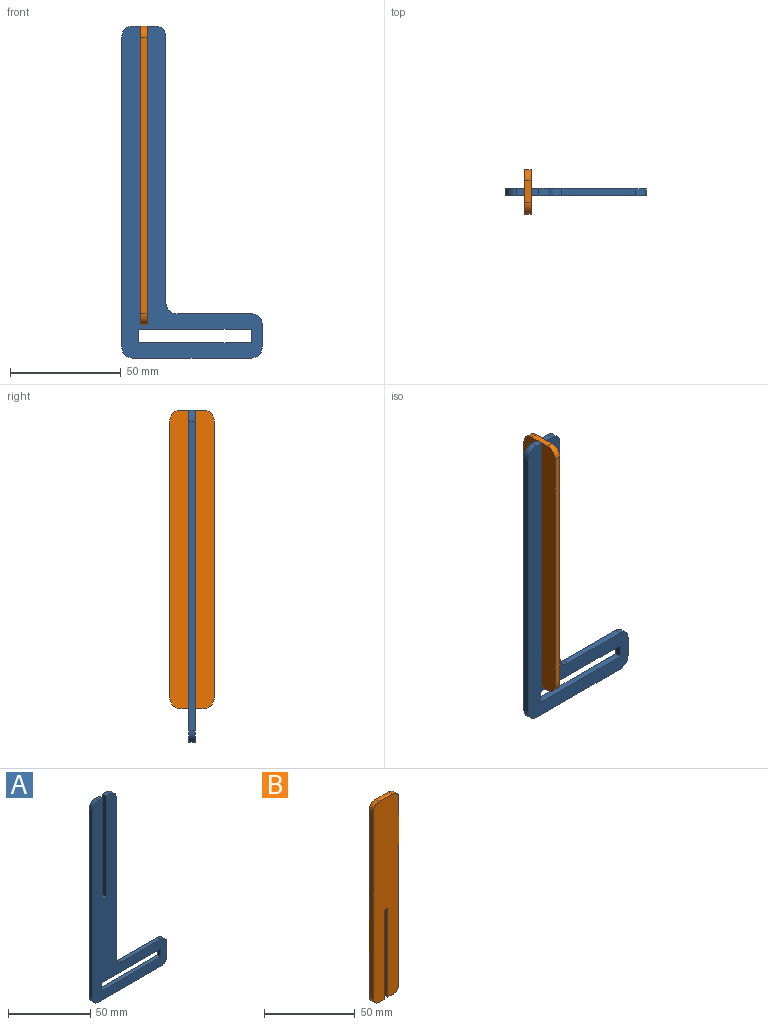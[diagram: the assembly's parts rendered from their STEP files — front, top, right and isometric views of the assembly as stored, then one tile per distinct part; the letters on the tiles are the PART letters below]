
ASSEMBLY  parts=2 mates=1
PART A: 22 faces, bbox 63.5x3x150 mm
  f0: plane 53.5x3mm, normal (0,0,-1), area 160.5mm2, adj f14,f15,f16,f21
  f1: plane 10x3mm, normal (1,0,0), area 30mm2, adj f14,f15,f16,f17
  f2: plane 33.5x3mm, normal (0,0,1), area 100.5mm2, adj f14,f15,f17,f18
  f3: plane 120x3mm, normal (1,0,0), area 360mm2, adj f14,f15,f18,f19
  f4: plane 3.5x3mm, normal (0,0,1), area 10.5mm2, adj f5,f14,f15,f19
  f5: plane 75x3mm, normal (-1,0,0), area 225mm2, adj f4,f6,f14,f15
  f6: plane 3x3mm, normal (0,0,1), area 9mm2, adj f5,f7,f14,f15
  f7: plane 75x3mm, normal (1,0,0), area 225mm2, adj f6,f8,f14,f15
  f8: plane 3.5x3mm, normal (0,0,1), area 10.5mm2, adj f7,f14,f15,f20
  f9: plane 6x3mm, normal (-1,0,0), area 18mm2, adj f10,f12,f14,f15
  f10: plane 51x3mm, normal (0,0,1), area 153mm2, adj f9,f11,f14,f15
  f11: plane 6x3mm, normal (1,0,0), area 18mm2, adj f10,f12,f14,f15
  f12: plane 51x3mm, normal (0,0,-1), area 153mm2, adj f9,f11,f14,f15
  f13: plane 140x3mm, normal (-1,0,0), area 420mm2, adj f14,f15,f20,f21
  f14: plane 150x63.5mm, normal (0,-1,0), area 3317.5mm2, adj f0,f1,f2,f3,f4,f5,f6,f7
  f15: plane 150x63.5mm, normal (0,1,0), area 3317.5mm2, adj f0,f1,f2,f3,f4,f5,f6,f7
  f16: cylinder r=5mm len=5mm, axis (0,1,0), area 23.6mm2, adj f0,f1,f14,f15
  f17: cylinder r=5mm len=5mm, axis (0,1,0), area 23.6mm2, adj f1,f2,f14,f15
  f18: cylinder r=5mm len=5mm, axis (0,-1,0), area 23.6mm2, adj f2,f3,f14,f15
  f19: cylinder r=5mm len=5mm, axis (0,-1,0), area 23.6mm2, adj f3,f4,f14,f15
  f20: cylinder r=5mm len=5mm, axis (0,-1,0), area 23.6mm2, adj f8,f13,f14,f15
  f21: cylinder r=5mm len=5mm, axis (0,1,0), area 23.6mm2, adj f0,f13,f14,f15
PART B: 14 faces, bbox 20x3x135 mm
  f0: plane 10x3mm, normal (0,0,1), area 30mm2, adj f8,f9,f10,f13
  f1: plane 125x3mm, normal (-1,0,0), area 375mm2, adj f8,f9,f10,f11
  f2: plane 3.5x3mm, normal (0,0,-1), area 10.5mm2, adj f3,f8,f9,f11
  f3: plane 60x3mm, normal (1,0,0), area 180mm2, adj f2,f4,f8,f9
  f4: plane 3x3mm, normal (0,0,-1), area 9mm2, adj f3,f5,f8,f9
  f5: plane 60x3mm, normal (-1,0,0), area 180mm2, adj f4,f6,f8,f9
  f6: plane 3.5x3mm, normal (0,0,-1), area 10.5mm2, adj f5,f8,f9,f12
  f7: plane 125x3mm, normal (1,0,0), area 375mm2, adj f8,f9,f12,f13
  f8: plane 135x20mm, normal (0,-1,0), area 2498.5mm2, adj f0,f1,f2,f3,f4,f5,f6,f7
  f9: plane 135x20mm, normal (0,1,0), area 2498.5mm2, adj f0,f1,f2,f3,f4,f5,f6,f7
  f10: cylinder r=5mm len=5mm, axis (0,1,0), area 23.6mm2, adj f0,f1,f8,f9
  f11: cylinder r=5mm len=5mm, axis (0,1,0), area 23.6mm2, adj f1,f2,f8,f9
  f12: cylinder r=5mm len=5mm, axis (0,1,0), area 23.6mm2, adj f6,f7,f8,f9
  f13: cylinder r=5mm len=5mm, axis (0,1,0), area 23.6mm2, adj f0,f7,f8,f9
PLACE A t=(-9.5,-11.95,80.69)mm
PLACE B rot(axis=(0,0,1),90deg) t=(-11,-13.45,80.69)mm
MATE fastened B.f4 <-> A.f6  axis (0,0,-1) through (-9.5,-13.45,155.69)mm
